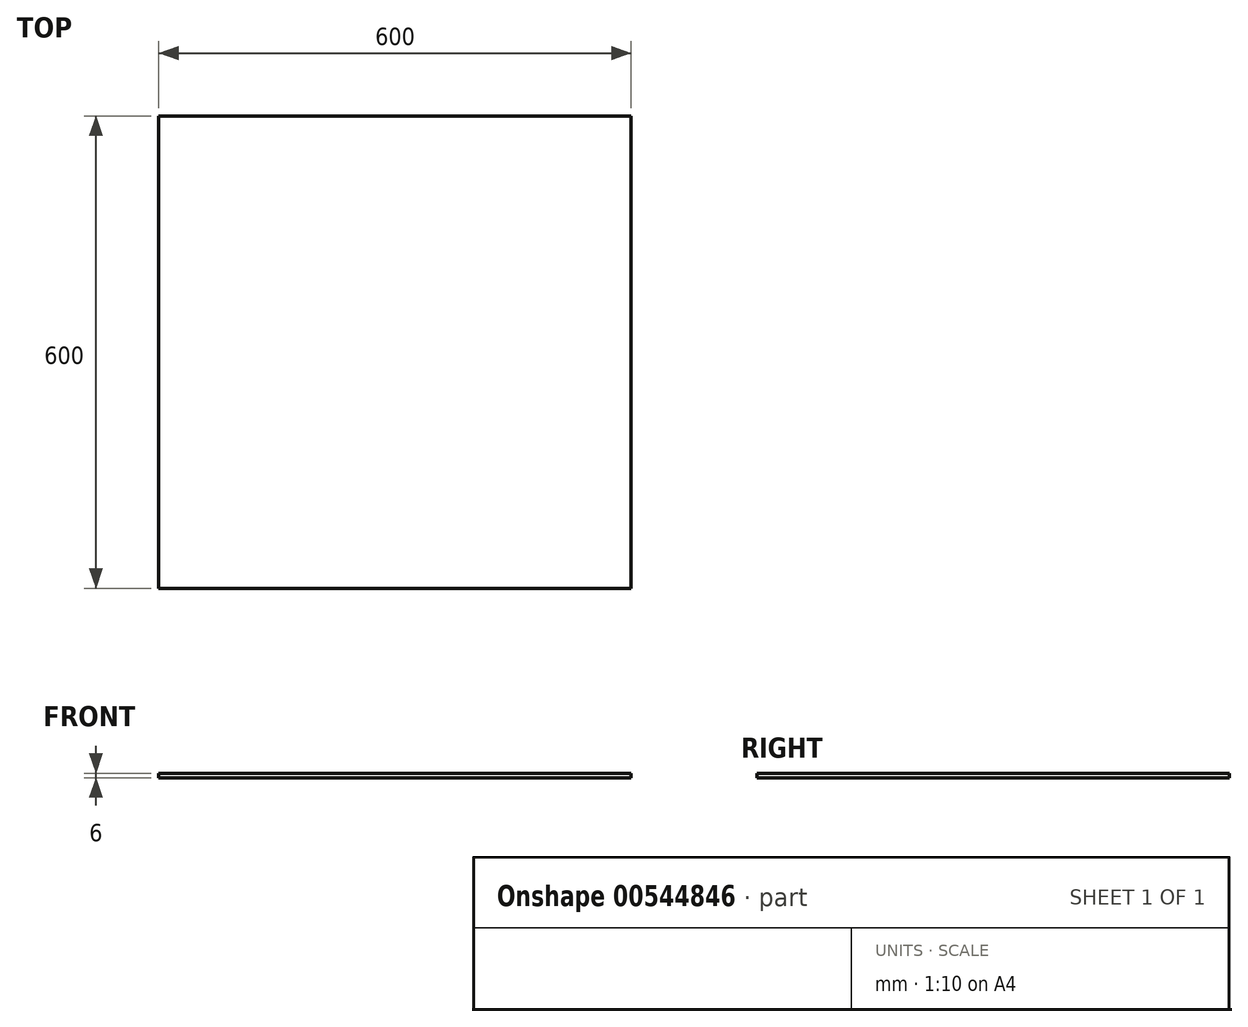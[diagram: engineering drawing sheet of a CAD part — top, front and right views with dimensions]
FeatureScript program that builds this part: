
annotation { "Feature Type Name" : "Feature", "Feature Type Description" : "" }
export const myFeature = defineFeature(function(context is Context, id is Id, definition is map)
    precondition{}
    {
        {
            var Q0;
            Q0=qCreatedBy(makeId("Top.planeOp"),FACE);
            var sketch = newSketch(context, id + "F0", { "sketchPlane" : qUnion([Q0])});
            skLineSegment(sketch, "E0.bottom", {"start": v(300, -300) * mm, "end": v(-300, -300) * mm});
            skLineSegment(sketch, "E0.top", {"start": v(300, 300) * mm, "end": v(-300, 300) * mm});
            skLineSegment(sketch, "E0.left", {"start": v(300, -300) * mm, "end": v(300, 300) * mm});
            skLineSegment(sketch, "E0.right", {"start": v(-300, -300) * mm, "end": v(-300, 300) * mm});
            skPoint(sketch, "E0.middle", {"position": v(0, 0) * mm});
            skSolve(sketch);
        }
        {
            var Q0;
            Q0 = qSketchRegion(id + "F0", true);
            extrude(context, id + "F1", {"entities" : qUnion([Q0]), "depth" : 6 * mm, "offsetDistance" : 25 * mm});
        }
    });
